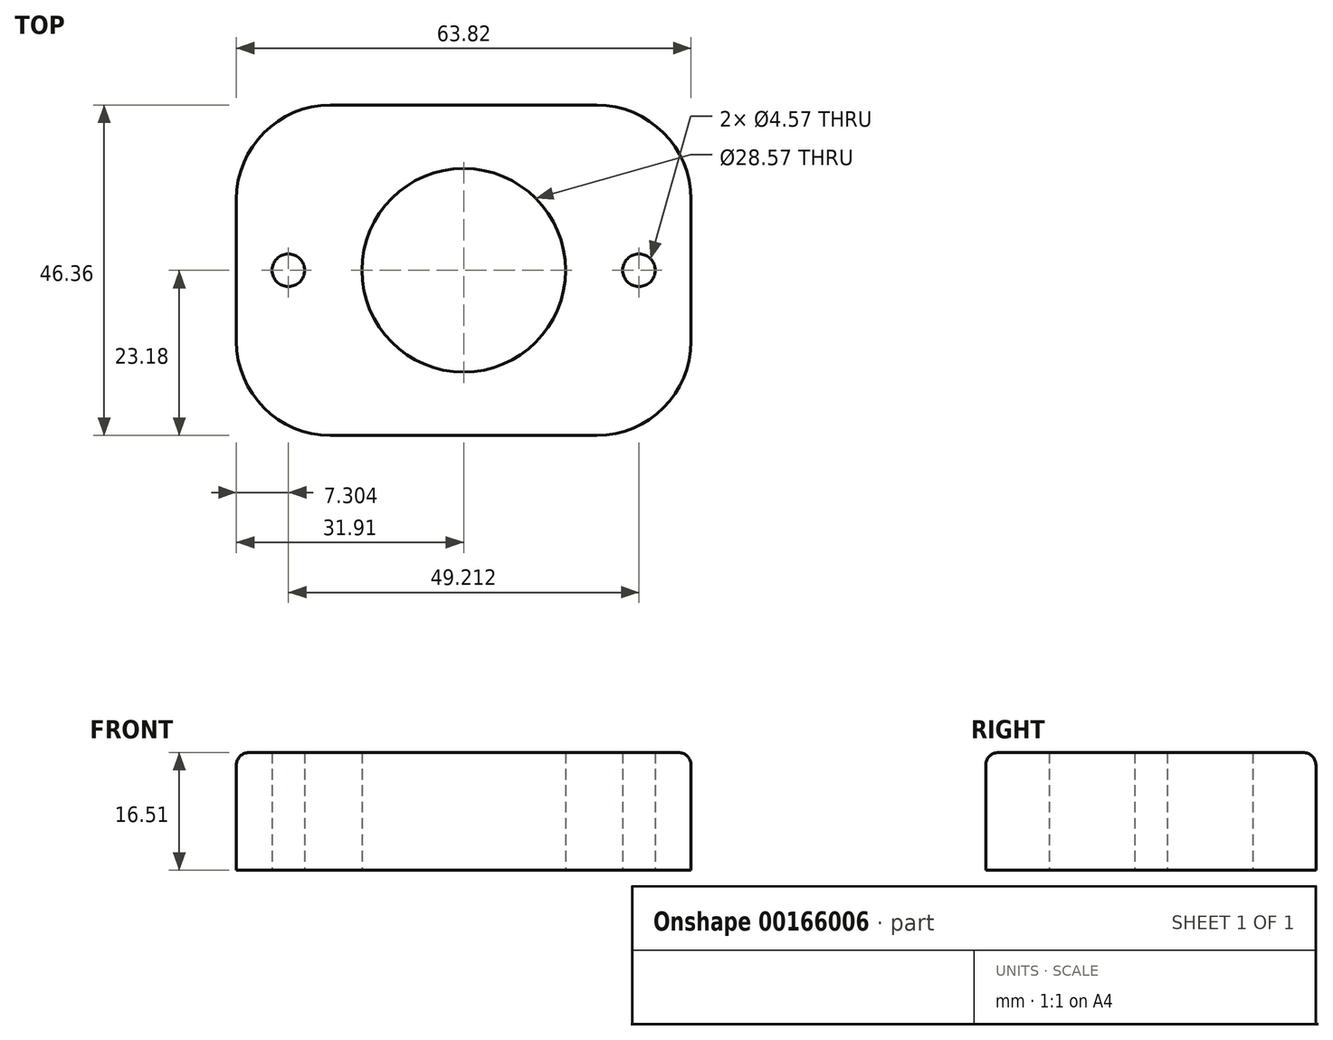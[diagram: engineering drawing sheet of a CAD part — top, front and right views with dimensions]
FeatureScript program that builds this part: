
annotation { "Feature Type Name" : "Feature", "Feature Type Description" : "" }
export const myFeature = defineFeature(function(context is Context, id is Id, definition is map)
    precondition{}
    {
        {
            var Q0;
            Q0=qCreatedBy(makeId("Top.planeOp"),FACE);
            var sketch = newSketch(context, id + "F0", { "sketchPlane" : qUnion([Q0])});
            skLineSegment(sketch, "E0.bottom", {"start": v(18.7, 20.64) * mm, "end": v(-18.7, 20.64) * mm});
            skLineSegment(sketch, "E0.top", {"start": v(18.7, -20.64) * mm, "end": v(-18.7, -20.64) * mm});
            skLineSegment(sketch, "E0.left", {"start": v(29.37, 9.97) * mm, "end": v(29.37, -9.97) * mm});
            skLineSegment(sketch, "E0.right", {"start": v(-29.37, 9.97) * mm, "end": v(-29.37, -9.97) * mm});
            skPoint(sketch, "E0.middle", {"position": v(0, 0) * mm});
            skCircle(sketch, "E1", {"center": v(0, 0) * mm, "radius": 14.29 * mm});
            skPoint(sketch, "E2", {"position": v(24.6, 0) * mm});
            skPoint(sketch, "E3", {"position": v(-24.6, 0) * mm});
            skCircle(sketch, "E4", {"center": v(24.6, 0) * mm, "radius": 2.29 * mm});
            skCircle(sketch, "E5", {"center": v(-24.6, 0) * mm, "radius": 2.29 * mm});
            skPoint(sketch, "E6.visualSharp", {"position": v(29.37, 20.64) * mm});
            skArc(sketch, "E6.filletArc", {"start": v(29.37, 9.97) * mm, "mid": v(26.24, 17.51) * mm, "end": v(18.7, 20.64) * mm});
            skPoint(sketch, "E7.visualSharp", {"position": v(29.37, -20.64) * mm});
            skArc(sketch, "E7.filletArc", {"start": v(18.7, -20.64) * mm, "mid": v(26.24, -17.51) * mm, "end": v(29.37, -9.97) * mm});
            skPoint(sketch, "E8.visualSharp", {"position": v(-29.37, 20.64) * mm});
            skArc(sketch, "E8.filletArc", {"start": v(-18.7, 20.64) * mm, "mid": v(-26.24, 17.51) * mm, "end": v(-29.37, 9.97) * mm});
            skPoint(sketch, "E9.visualSharp", {"position": v(-29.37, -20.64) * mm});
            skArc(sketch, "E9.filletArc", {"start": v(-29.37, -9.97) * mm, "mid": v(-26.24, -17.51) * mm, "end": v(-18.7, -20.64) * mm});
            skArc(sketch, "E10.0", {"start": v(18.7, -23.18) * mm, "mid": v(28.04, -19.3) * mm, "end": v(31.9, -9.97) * mm});
            skLineSegment(sketch, "E10.1", {"start": v(31.9, 9.97) * mm, "end": v(31.9, -9.97) * mm});
            skLineSegment(sketch, "E10.2", {"start": v(18.7, -23.18) * mm, "end": v(-18.7, -23.18) * mm});
            skArc(sketch, "E10.3", {"start": v(31.9, 9.97) * mm, "mid": v(28.04, 19.3) * mm, "end": v(18.7, 23.18) * mm});
            skArc(sketch, "E10.4", {"start": v(-31.9, -9.97) * mm, "mid": v(-28.04, -19.3) * mm, "end": v(-18.7, -23.18) * mm});
            skLineSegment(sketch, "E10.5", {"start": v(-31.9, 9.97) * mm, "end": v(-31.9, -9.97) * mm});
            skArc(sketch, "E10.6", {"start": v(-18.7, 23.18) * mm, "mid": v(-28.04, 19.3) * mm, "end": v(-31.9, 9.97) * mm});
            skLineSegment(sketch, "E10.7", {"start": v(18.7, 23.18) * mm, "end": v(-18.7, 23.18) * mm});
            skSolve(sketch);
        }
        {
            var Q0;
            Q0=makeQuery(id+"F0.imprint","IMPRINT",FACE,{"disambiguationData":[TD([[makeQuery(id+"F0.imprint","IMPRINT",EDGE,{"derivedFrom":sQuery(id+"F0.wireOp",EDGE,"E0.bottom")}),1.0]])]});
            var Q1;
            Q1=makeQuery(id+"F0.imprint","IMPRINT",FACE,{"disambiguationData":[TD([[makeQuery(id+"F0.imprint","IMPRINT",EDGE,{"derivedFrom":sQuery(id+"F0.wireOp",EDGE,"E0.bottom")}),-1.0]])]});
            extrude(context, id + "F1", {"entities" : qUnion([Q0, Q1]), "depth" : 16.5 * mm});
        }
        {
            var Q0;
            Q0=makeQuery(id+"F1.opExtrude","CAP_EDGE",EDGE,{"disambiguationData":[OSD([sQuery(id+"F0.wireOp",EDGE,"E10.3")])],"isStart":false});
            fillet(context, id + "F2", {"entities" : qUnion([Q0]), "radius" : 1.78 * mm, "tangentPropagation" : true, "allowEdgeOverflow" : false});
        }
    });
